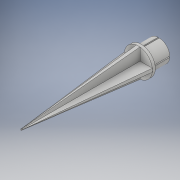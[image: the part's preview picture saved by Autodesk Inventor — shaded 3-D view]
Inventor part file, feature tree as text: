
AUTODESK INVENTOR PART (.ipt)
format: ipt  version: 2019.2 (Build 232265000, 265)  size: 190,464 bytes
history: native  units: in
note: dims shown in document units (in); Inventor stores cm internally (conversion verified against a paired STEP export)
features: sketch x4, extrude x3, plane x1, loft x1
ambient origin geometry x8: Origin, YZ Plane, XZ Plane, XY Plane, X Axis, Y Axis, Z Axis, Center Point
bodies: Solid1 (feature_tree)
feature tree (9):
  extrude  "Extrusion1"  Depth=0.125in
  extrude  "Extrusion2"  Depth=0.94in
  sketch  "Sketch4"  dims[d4=0.75in d5=0.0in]
  plane  "Work Plane1"
  loft  "Loft1"
  extrude  "Extrusion3"  Depth=0.05in
  sketch  "Sketch1"  dims[d0=1.2in d1=0.125in]
  sketch  "Sketch2"  dims[d2=0.0in d3=0.94in]
  sketch  "Sketch6"  dims[d7=0.6in d8=0.6in d31=0.15in d10=0.075in d11=0.15in d12=5.0in d14=0.0in d15=90.0deg d16=0.0in d17=90.0deg d18=0.05in d19=1.04in d20=0.65in d21=0.0in d32=0.05in]
